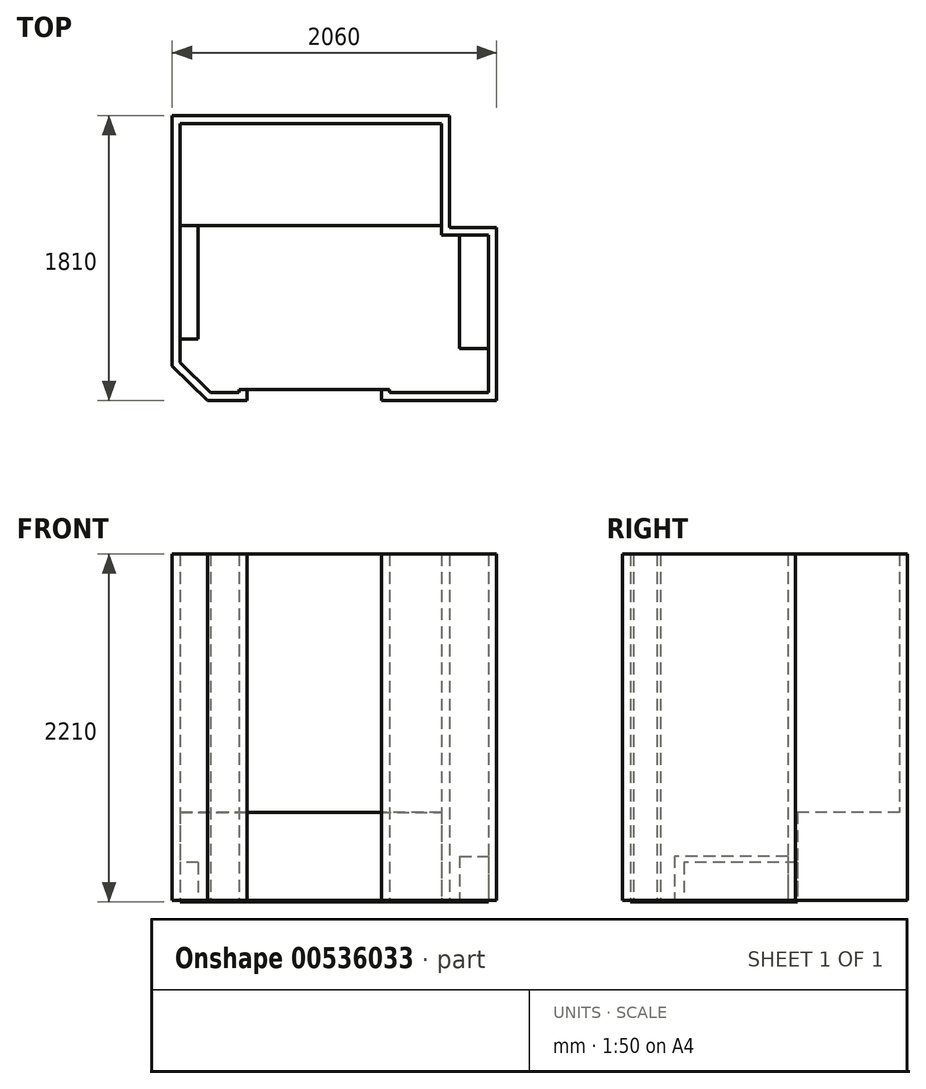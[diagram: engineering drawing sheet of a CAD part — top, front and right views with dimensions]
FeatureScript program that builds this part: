
annotation { "Feature Type Name" : "Feature", "Feature Type Description" : "" }
export const myFeature = defineFeature(function(context is Context, id is Id, definition is map)
    precondition{}
    {
        {
            var Q0;
            Q0=qCreatedBy(makeId("Top.planeOp"),FACE);
            var sketch = newSketch(context, id + "F0", { "sketchPlane" : qUnion([Q0])});
            skLineSegment(sketch, "E0", {"start": v(0, 0) * mm, "end": v(1660, 0) * mm});
            skLineSegment(sketch, "E1", {"start": v(0, 0) * mm, "end": v(0, -1520) * mm});
            skLineSegment(sketch, "E2", {"start": v(1660, 0) * mm, "end": v(1660, -710) * mm});
            skLineSegment(sketch, "E3", {"start": v(1660, -710) * mm, "end": v(1960, -710) * mm});
            skLineSegment(sketch, "E4", {"start": v(1960, -710) * mm, "end": v(1960, -1710) * mm});
            skLineSegment(sketch, "E5", {"start": v(1960, -1710) * mm, "end": v(1330, -1710) * mm});
            skLineSegment(sketch, "E6", {"start": v(1330, -1710) * mm, "end": v(1330, -1690) * mm});
            skLineSegment(sketch, "E7", {"start": v(1330, -1690) * mm, "end": v(375, -1690) * mm});
            skLineSegment(sketch, "E8", {"start": v(375, -1690) * mm, "end": v(375, -1710) * mm});
            skLineSegment(sketch, "E9", {"start": v(375, -1710) * mm, "end": v(195, -1710) * mm});
            skLineSegment(sketch, "E10", {"start": v(195, -1710) * mm, "end": v(0, -1520) * mm});
            skLineSegment(sketch, "E11.0", {"start": v(2010, -1760) * mm, "end": v(1280, -1760) * mm});
            skLineSegment(sketch, "E11.1", {"start": v(2010, -660) * mm, "end": v(2010, -1760) * mm});
            skLineSegment(sketch, "E11.2", {"start": v(1710, -660) * mm, "end": v(2010, -660) * mm});
            skLineSegment(sketch, "E11.3", {"start": v(1710, 50) * mm, "end": v(1710, -660) * mm});
            skLineSegment(sketch, "E11.4", {"start": v(-50, 50) * mm, "end": v(1710, 50) * mm});
            skLineSegment(sketch, "E11.5", {"start": v(1280, -1760) * mm, "end": v(1280, -1740) * mm});
            skLineSegment(sketch, "E11.7", {"start": v(425, -1740) * mm, "end": v(425, -1760) * mm});
            skLineSegment(sketch, "E11.8", {"start": v(425, -1760) * mm, "end": v(174.67, -1760) * mm});
            skLineSegment(sketch, "E11.9", {"start": v(174.67, -1760) * mm, "end": v(-50, -1541.1) * mm});
            skLineSegment(sketch, "E11.10", {"start": v(-50, 50) * mm, "end": v(-50, -1541.1) * mm});
            skLineSegment(sketch, "E12", {"start": v(425, -1740) * mm, "end": v(425, -1690) * mm});
            skLineSegment(sketch, "E13", {"start": v(1280, -1740) * mm, "end": v(1280, -1690) * mm});
            skLineSegment(sketch, "E14", {"start": v(1660, -710) * mm, "end": v(1660, -650) * mm, "construction": true});
            skLineSegment(sketch, "E15", {"start": v(1660, -650) * mm, "end": v(0, -650) * mm});
            skLineSegment(sketch, "E16", {"start": v(0, -650) * mm, "end": v(115, -650) * mm, "construction": true});
            skLineSegment(sketch, "E17", {"start": v(115, -650) * mm, "end": v(115, -1370) * mm});
            skLineSegment(sketch, "E18", {"start": v(115, -1370) * mm, "end": v(0, -1370) * mm});
            skLineSegment(sketch, "E19", {"start": v(1960, -710) * mm, "end": v(1775, -710) * mm, "construction": true});
            skLineSegment(sketch, "E20", {"start": v(1775, -710) * mm, "end": v(1775, -1430) * mm});
            skLineSegment(sketch, "E21", {"start": v(1775, -1430) * mm, "end": v(1960, -1430) * mm});
            skSolve(sketch);
        }
        {
            var Q0;
            Q0=makeQuery(id+"F0.imprint","IMPRINT",FACE,{"disambiguationData":[TD([[makeQuery(id+"F0.imprint","IMPRINT",EDGE,{"derivedFrom":sQuery(id+"F0.wireOp",EDGE,"E0")}),1.0]])]});
            extrude(context, id + "F1", {"entities" : qUnion([Q0]), "depth" : 2200 * mm, "offsetDistance" : 25 * mm});
        }
        {
            var Q0;
            {var subQ0=sQuery(id+"F0.wireOp",EDGE,"E0");Q0=makeQuery(id+"F0.imprint","IMPRINT",FACE,{"disambiguationData":[TD([[makeQuery(id+"F0.imprint","IMPRINT",EDGE,{"derivedFrom":subQ0}),-1.0]])]});}
            extrude(context, id + "F2", {"entities" : qUnion([Q0]), "operationType" : NewBodyOperationType.ADD, "depth" : 560 * mm, "offsetDistance" : 25 * mm});
        }
        {
            var Q0;
            {var subQ4=sQuery(id+"F0.wireOp",EDGE,"E17");Q0=makeQuery(id+"F0.imprint","IMPRINT",FACE,{"disambiguationData":[TD([[makeQuery(id+"F0.imprint","IMPRINT",EDGE,{"derivedFrom":subQ4}),-1.0]])]});}
            extrude(context, id + "F3", {"entities" : qUnion([Q0]), "operationType" : NewBodyOperationType.ADD, "depth" : 240 * mm, "offsetDistance" : 25 * mm});
        }
        {
            var Q0;
            {var subQ3=sQuery(id+"F0.wireOp",EDGE,"E20");Q0=makeQuery(id+"F0.imprint","IMPRINT",FACE,{"disambiguationData":[TD([[makeQuery(id+"F0.imprint","IMPRINT",EDGE,{"derivedFrom":subQ3}),1.0]])]});}
            extrude(context, id + "F4", {"entities" : qUnion([Q0]), "operationType" : NewBodyOperationType.ADD, "depth" : 280 * mm, "offsetDistance" : 25 * mm});
        }
        {
            var Q0;
            {var subQ7=sQuery(id+"F0.wireOp",EDGE,"E5");Q0=makeQuery(id+"F0.imprint","IMPRINT",FACE,{"disambiguationData":[TD([[makeQuery(id+"F0.imprint","IMPRINT",EDGE,{"derivedFrom":subQ7}),-1.0]])]});}
            extrude(context, id + "F5", {"entities" : qUnion([Q0]), "oppositeDirection" : true, "depth" : 10 * mm, "offsetDistance" : 25 * mm});
        }
    });
